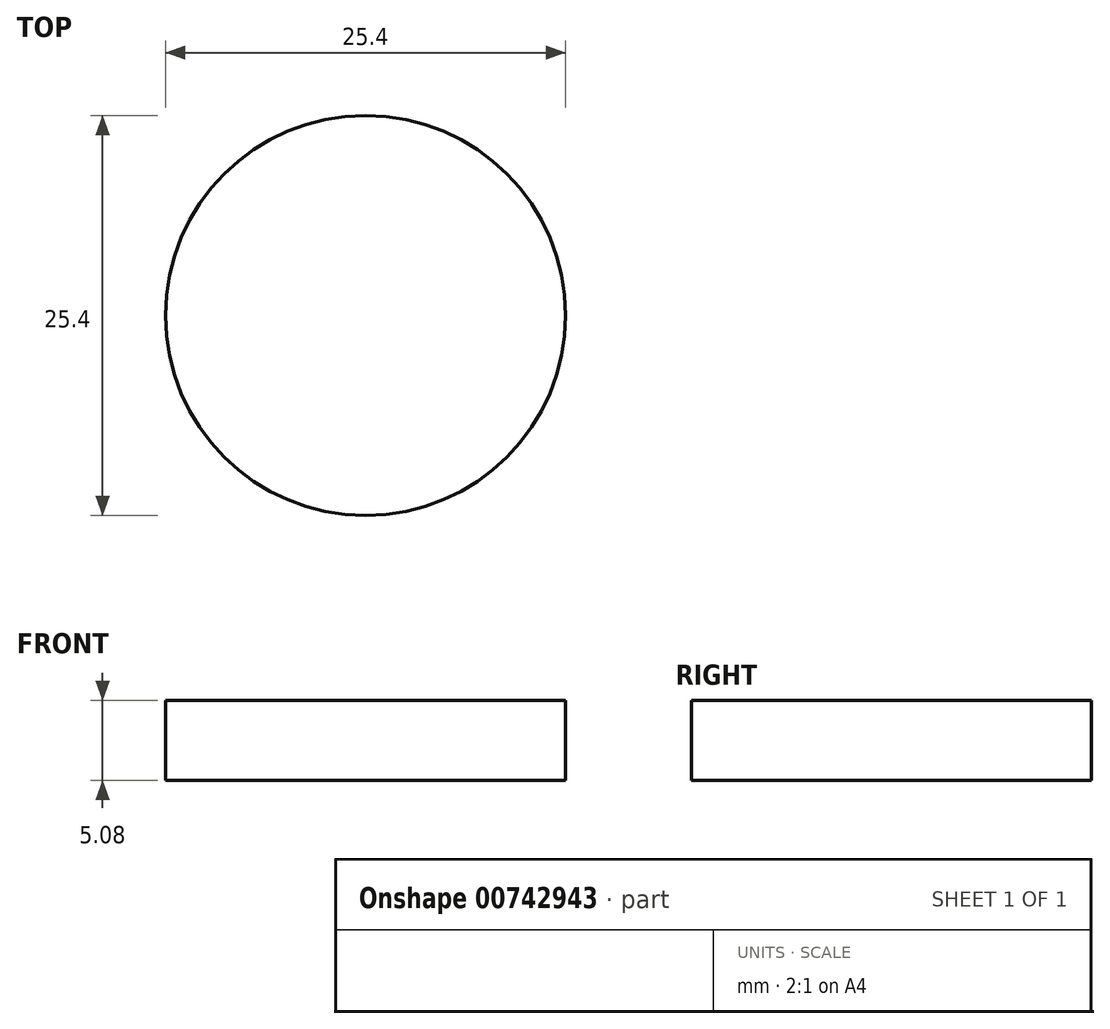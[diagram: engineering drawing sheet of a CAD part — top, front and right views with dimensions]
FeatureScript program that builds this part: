
annotation { "Feature Type Name" : "Feature", "Feature Type Description" : "" }
export const myFeature = defineFeature(function(context is Context, id is Id, definition is map)
    precondition{}
    {
        {
            var Q0;
            Q0=qCreatedBy(makeId("Top.planeOp"),FACE);
            var sketch = newSketch(context, id + "F0", { "sketchPlane" : qUnion([Q0])});
            skCircle(sketch, "E0", {"center": v(0, 0) * mm, "radius": 12.7 * mm});
            skSolve(sketch);
        }
        {
            var Q0;
            Q0=makeQuery(id+"F0.imprint","IMPRINT",FACE,{"disambiguationData":[TD([[makeQuery(id+"F0.imprint","IMPRINT",EDGE,{"derivedFrom":sQuery(id+"F0.wireOp",EDGE,"E0")}),1.0]])]});
            extrude(context, id + "F1", {"entities" : qUnion([Q0]), "depth" : 5.08 * mm, "offsetDistance" : 25.4 * mm});
        }
    });
